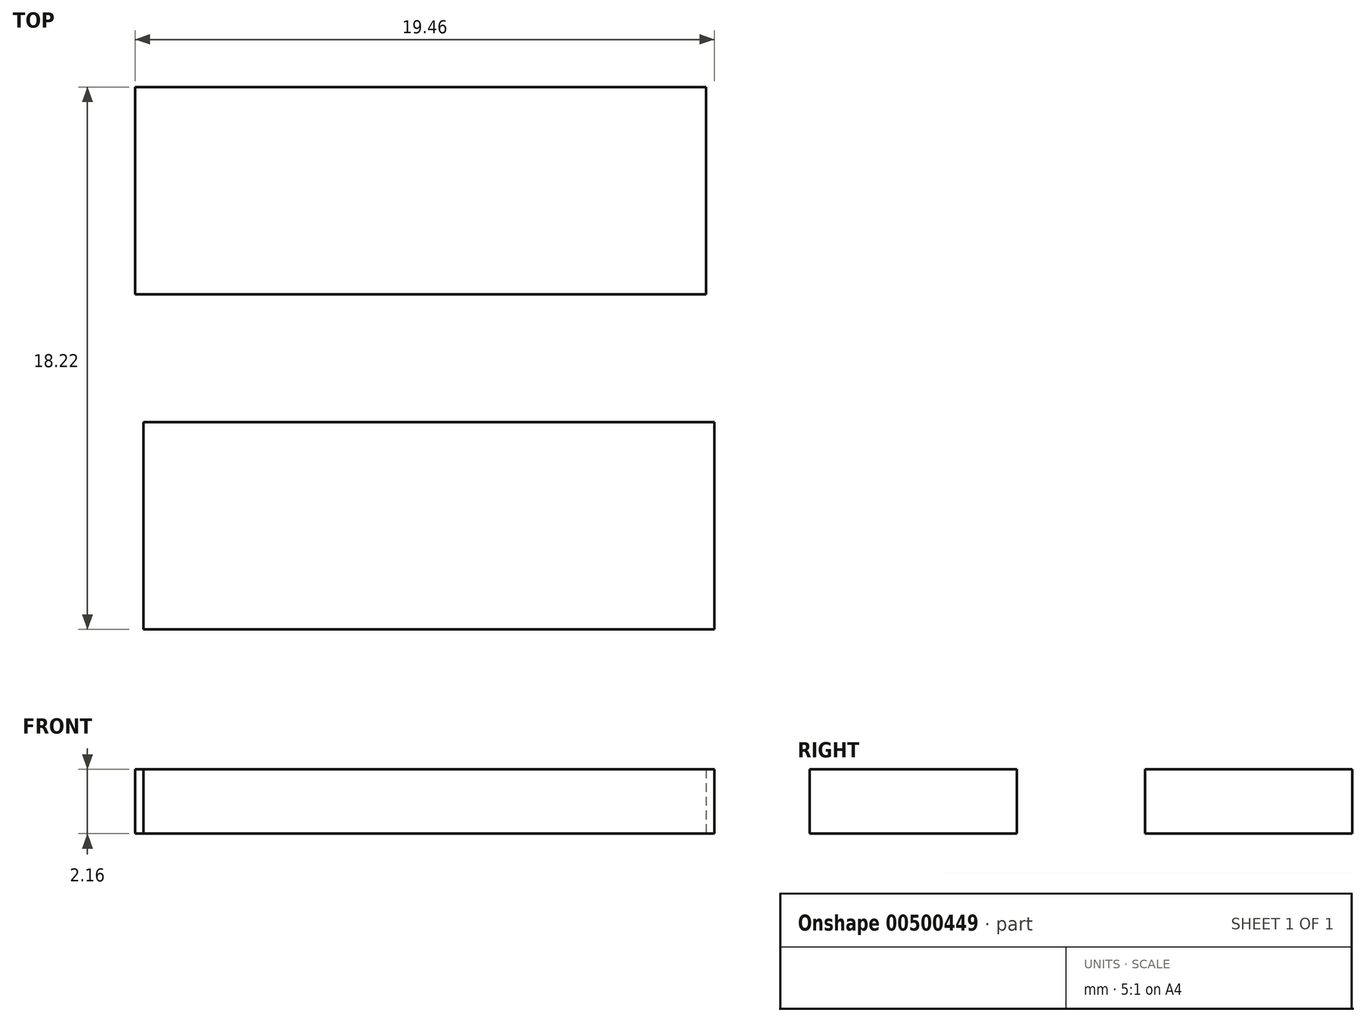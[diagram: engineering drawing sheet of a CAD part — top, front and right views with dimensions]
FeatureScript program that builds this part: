
annotation { "Feature Type Name" : "Feature", "Feature Type Description" : "" }
export const myFeature = defineFeature(function(context is Context, id is Id, definition is map)
    precondition{}
    {
        {
            var Q0;
            Q0=qCreatedBy(makeId("Top.planeOp"),FACE);
            var sketch = newSketch(context, id + "F0", { "sketchPlane" : qUnion([Q0])});
            skLineSegment(sketch, "E0.bottom", {"start": v(6.78, -4.3) * mm, "end": v(25.96, -4.3) * mm});
            skLineSegment(sketch, "E0.top", {"start": v(6.78, -11.26) * mm, "end": v(25.96, -11.26) * mm});
            skLineSegment(sketch, "E0.left", {"start": v(6.78, -4.3) * mm, "end": v(6.78, -11.26) * mm});
            skLineSegment(sketch, "E0.right", {"start": v(25.96, -4.3) * mm, "end": v(25.96, -11.26) * mm});
            skLineSegment(sketch, "E1.bottom", {"start": v(6.5, 0) * mm, "end": v(25.68, 0) * mm});
            skLineSegment(sketch, "E1.top", {"start": v(6.5, 6.96) * mm, "end": v(25.68, 6.96) * mm});
            skLineSegment(sketch, "E1.left", {"start": v(6.5, 0) * mm, "end": v(6.5, 6.96) * mm});
            skLineSegment(sketch, "E1.right", {"start": v(25.68, 0) * mm, "end": v(25.68, 6.96) * mm});
            skSolve(sketch);
        }
        {
            var Q0;
            Q0=makeQuery(id+"F0.imprint","IMPRINT",FACE,{"disambiguationData":[TD([[makeQuery(id+"F0.imprint","IMPRINT",EDGE,{"derivedFrom":sQuery(id+"F0.wireOp",EDGE,"E0.bottom")}),-1.0]])]});
            var Q1;
            Q1=makeQuery(id+"F0.imprint","IMPRINT",FACE,{"disambiguationData":[TD([[makeQuery(id+"F0.imprint","IMPRINT",EDGE,{"derivedFrom":sQuery(id+"F0.wireOp",EDGE,"E1.bottom")}),1.0]])]});
            extrude(context, id + "F1", {"entities" : qUnion([Q0, Q1]), "depth" : 2.16 * mm});
        }
    });
